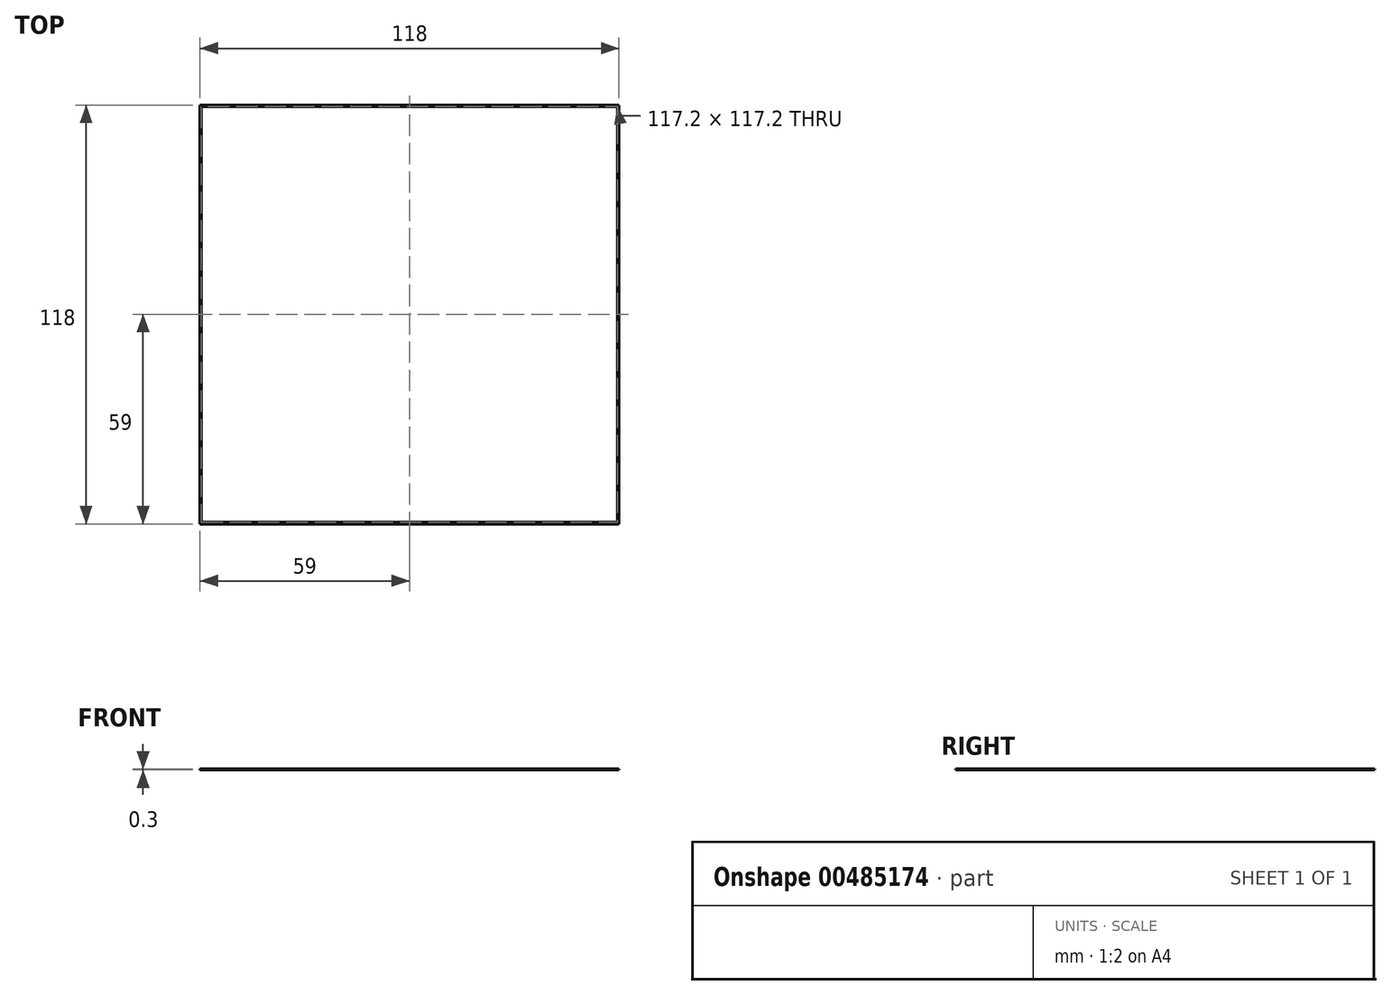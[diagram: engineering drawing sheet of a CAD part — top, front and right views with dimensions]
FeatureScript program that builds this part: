
annotation { "Feature Type Name" : "Feature", "Feature Type Description" : "" }
export const myFeature = defineFeature(function(context is Context, id is Id, definition is map)
    precondition{}
    {
        {
            var Q0;
            Q0=qCreatedBy(makeId("Top.planeOp"),FACE);
            var sketch = newSketch(context, id + "F0", { "sketchPlane" : qUnion([Q0])});
            skLineSegment(sketch, "E0.bottom", {"start": v(0, 0) * mm, "end": v(118, 0) * mm});
            skLineSegment(sketch, "E0.top", {"start": v(0, 118) * mm, "end": v(118, 118) * mm});
            skLineSegment(sketch, "E0.left", {"start": v(0, 0) * mm, "end": v(0, 118) * mm});
            skLineSegment(sketch, "E0.right", {"start": v(118, 0) * mm, "end": v(118, 118) * mm});
            skLineSegment(sketch, "E1.0", {"start": v(0.4, 0.4) * mm, "end": v(117.6, 0.4) * mm});
            skLineSegment(sketch, "E1.1", {"start": v(0.4, 0.4) * mm, "end": v(0.4, 117.6) * mm});
            skLineSegment(sketch, "E1.2", {"start": v(0.4, 117.6) * mm, "end": v(117.6, 117.6) * mm});
            skLineSegment(sketch, "E1.3", {"start": v(117.6, 0.4) * mm, "end": v(117.6, 117.6) * mm});
            skSolve(sketch);
        }
        {
            var Q0;
            Q0=makeQuery(id+"F0.imprint","IMPRINT",FACE,{"disambiguationData":[TD([[makeQuery(id+"F0.imprint","IMPRINT",EDGE,{"derivedFrom":sQuery(id+"F0.wireOp",EDGE,"E0.bottom")}),1.0]])]});
            extrude(context, id + "F1", {"entities" : qUnion([Q0]), "depth" : .3 * mm, "offsetDistance" : 25 * mm});
        }
    });
